# Revit family: ASL_Plus_Series_Head & Floor_Track_90mm_Stud
name_source: partatom
category: Detail Items
revit_build: Autodesk Revit 2018 (Build: 20170223_1515(x64)
units: mm (PartAtom-declared; Revit-internal decimal feet)

## family parameters
Rotate with component = No
Section Shape = Not Defined
Shared = Yes

## types (4) — shared parameters
Manufacturer = Aluminate Solutions Limited
Technical Info = www.aluminate.nz
Type Comments = Plus Series

## per-type parameters (varying)
| type | Headsection&Floor Track_ASL_756 | Headsection_ASL_741 | Plasterboard 13mm | Plasterboard Depth | Steel Stud 64mm | Steel Stud 89mm |
| 25mm Negative Head & Floor Track 64mm Stud 2x13mm Gib Ext 13mm Gib Int | Yes | No | Yes | 60 mm | Yes | No |
| 13mm Negative Head & Floor Track 64mm Stud 2x13mm Gib Ext 13mm Gib Int | No | Yes | Yes | 47 mm | Yes | No |
| 25mm Negative Head & Floor Track 90mm Stud 13mm Gib BS | Yes | No | No | 60 mm | No | Yes |
| Negative Head 90mm Stud 13mm Gib BS | No | Yes | No | 47 mm | No | Yes |

## geometry (parser evidence)
native form markers: Sweep x5
no freeform markers — native parametric forms only
